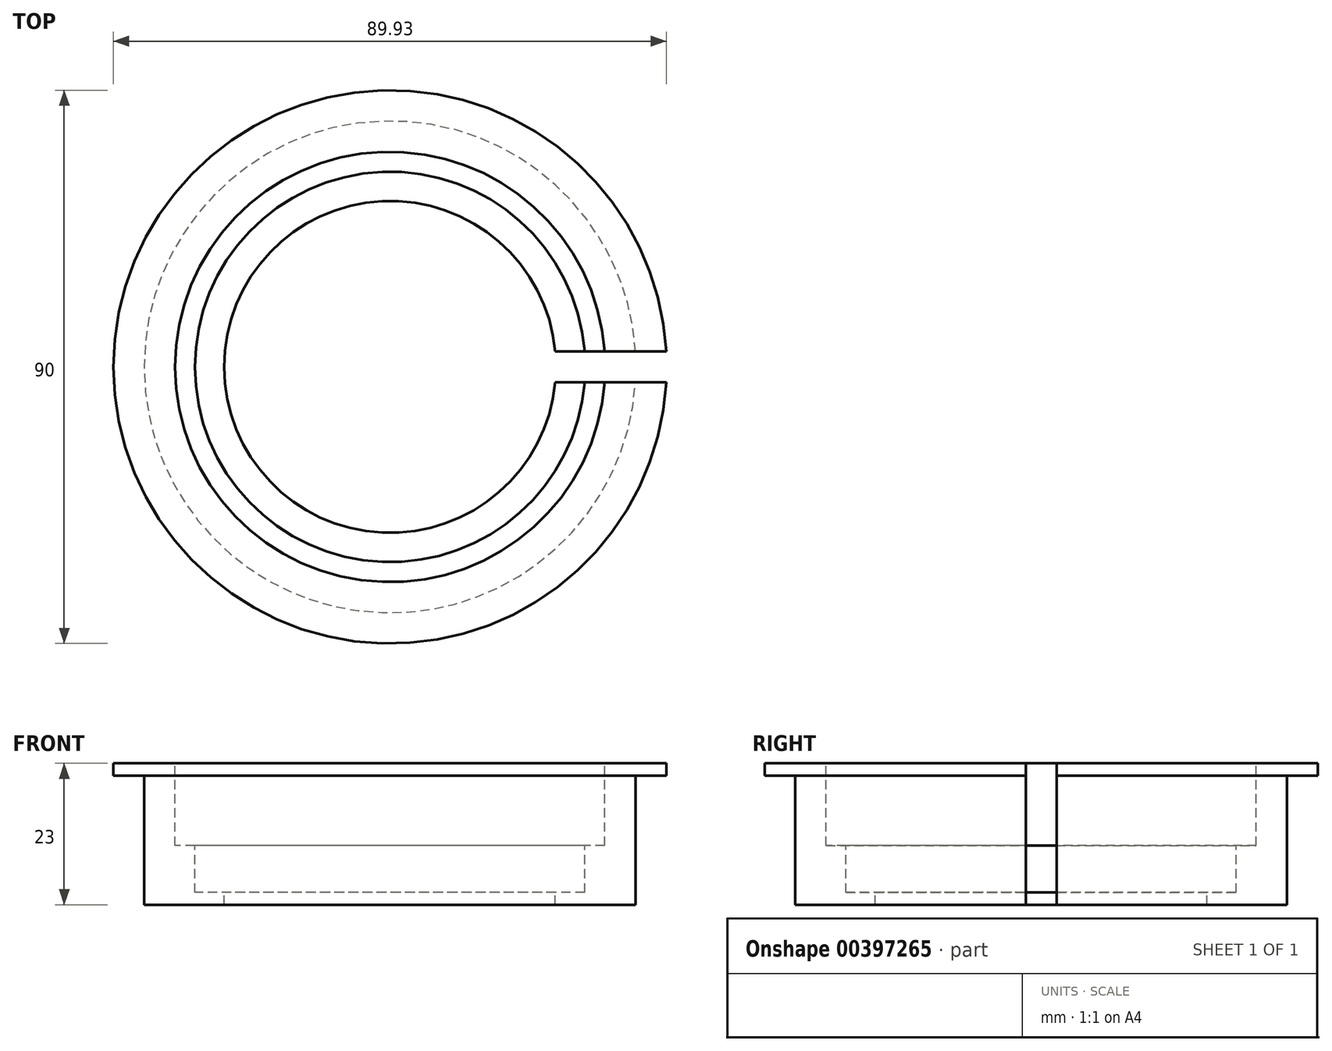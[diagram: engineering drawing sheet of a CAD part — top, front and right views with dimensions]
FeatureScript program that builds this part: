
annotation { "Feature Type Name" : "Feature", "Feature Type Description" : "" }
export const myFeature = defineFeature(function(context is Context, id is Id, definition is map)
    precondition{}
    {
        {
            var Q0;
            Q0=qCreatedBy(makeId("Top.planeOp"),FACE);
            var sketch = newSketch(context, id + "F0", { "sketchPlane" : qUnion([Q0])});
            skCircle(sketch, "E0", {"center": v(0, 0) * mm, "radius": 45 * mm});
            skSolve(sketch);
        }
        {
            var Q0;
            Q0 = qSketchRegion(id + "F0", true);
            extrude(context, id + "F1", {"entities" : qUnion([Q0]), "depth" : 23 * mm});
        }
        {
            var Q0;
            Q0=makeQuery(id+"F1.opExtrude","CAP_FACE",FACE,{"disambiguationData":[OSD([sQuery(id+"F0.wireOp",EDGE,"E0")])],"isStart":false});
            var sketch = newSketch(context, id + "F2", { "sketchPlane" : qUnion([Q0])});
            skCircle(sketch, "E1", {"center": v(0, 0) * mm, "radius": 35 * mm});
            skSolve(sketch);
        }
        {
            var Q0;
            Q0 = qSketchRegion(id + "F2", true);
            extrude(context, id + "F3", {"entities" : qUnion([Q0]), "operationType" : NewBodyOperationType.REMOVE, "oppositeDirection" : true, "depth" : 13.4 * mm});
        }
        {
            var Q0;
            Q0=makeQuery(id+"F3.boolean.opBoolean","COPY",FACE,{"derivedFrom":makeQuery(id+"F3.opExtrude","CAP_FACE",FACE,{"disambiguationData":[OSD([sQuery(id+"F2.wireOp",EDGE,"E1")])],"isStart":false})});
            var sketch = newSketch(context, id + "F4", { "sketchPlane" : qUnion([Q0])});
            skCircle(sketch, "E2", {"center": v(0, 0) * mm, "radius": 31.75 * mm});
            skSolve(sketch);
        }
        {
            var Q0;
            Q0 = qSketchRegion(id + "F4", true);
            extrude(context, id + "F5", {"entities" : qUnion([Q0]), "operationType" : NewBodyOperationType.REMOVE, "oppositeDirection" : true, "depth" : 7.6 * mm});
        }
        {
            var Q0;
            Q0=makeQuery(id+"F5.boolean.opBoolean","COPY",FACE,{"derivedFrom":makeQuery(id+"F5.opExtrude","CAP_FACE",FACE,{"disambiguationData":[OSD([sQuery(id+"F4.wireOp",EDGE,"E2")])],"isStart":false})});
            var sketch = newSketch(context, id + "F6", { "sketchPlane" : qUnion([Q0])});
            skCircle(sketch, "E3", {"center": v(0, 0) * mm, "radius": 27 * mm});
            skSolve(sketch);
        }
        {
            var Q0;
            Q0 = qSketchRegion(id + "F6", true);
            extrude(context, id + "F7", {"entities" : qUnion([Q0]), "operationType" : NewBodyOperationType.REMOVE, "endBound" : BoundingType.THROUGH_ALL, "oppositeDirection" : true, "depth" : 25 * mm});
        }
        {
            var Q0;
            Q0=makeQuery(id+"F1.opExtrude","CAP_FACE",FACE,{"disambiguationData":[OSD([sQuery(id+"F0.wireOp",EDGE,"E0")])],"isStart":true});
            var sketch = newSketch(context, id + "F8", { "sketchPlane" : qUnion([Q0])});
            skCircle(sketch, "E4", {"center": v(0, 0) * mm, "radius": 45 * mm});
            skCircle(sketch, "E5", {"center": v(0, 0) * mm, "radius": 40 * mm});
            skSolve(sketch);
        }
        {
            var Q0;
            Q0 = qSketchRegion(id + "F8", true);
            extrude(context, id + "F9", {"entities" : qUnion([Q0]), "operationType" : NewBodyOperationType.REMOVE, "oppositeDirection" : true, "depth" : 21 * mm});
        }
        {
            var Q0;
            Q0=makeQuery(id+"F1.opExtrude","CAP_FACE",FACE,{"disambiguationData":[OSD([sQuery(id+"F0.wireOp",EDGE,"E0")])],"isStart":false});
            var sketch = newSketch(context, id + "F10", { "sketchPlane" : qUnion([Q0])});
            skLineSegment(sketch, "E6", {"start": v(0, 0) * mm, "end": v(45, 0) * mm, "construction": true});
            skLineSegment(sketch, "E7.bottom", {"start": v(50, -2.5) * mm, "end": v(50, 2.5) * mm});
            skLineSegment(sketch, "E7.top", {"start": v(20, -2.5) * mm, "end": v(20, 2.5) * mm});
            skLineSegment(sketch, "E7.left", {"start": v(50, -2.5) * mm, "end": v(20, -2.5) * mm});
            skLineSegment(sketch, "E7.right", {"start": v(50, 2.5) * mm, "end": v(20, 2.5) * mm});
            skPoint(sketch, "E7.middle", {"position": v(35, 0) * mm});
            skSolve(sketch);
        }
        {
            var Q0;
            Q0 = qSketchRegion(id + "F10", true);
            extrude(context, id + "F11", {"entities" : qUnion([Q0]), "operationType" : NewBodyOperationType.REMOVE, "endBound" : BoundingType.THROUGH_ALL, "oppositeDirection" : true, "depth" : 25 * mm});
        }
    });
